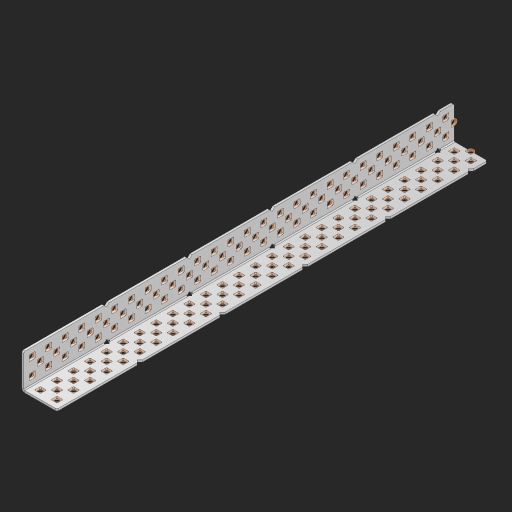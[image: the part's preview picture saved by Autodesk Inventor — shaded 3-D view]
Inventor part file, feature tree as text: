
AUTODESK INVENTOR PART (.ipt)
format: ipt  version: 2023 (Build 270158000, 158)  size: 1,877,504 bytes
history: native  units: in
note: dims shown in document units (in); Inventor stores cm internally (conversion verified against a paired STEP export)
features: other x162, extrude x154, sheet_metal_op x8, sketch x7, pattern_linear x2, mirror x1, chamfer x1
ambient origin geometry x8: Origin, YZ Plane, XZ Plane, XY Plane, X Axis, Y Axis, Z Axis, Center Point
bodies: Solid1 (feature_tree), Body (feature_tree)
feature tree (335):
  sheet_metal_op  "Flanges"
  sheet_metal_op  "Body Pattern"
  pattern_linear  "Center Pattern"  Spacing1=1.0in  [1 undecoded]
  other  "Arc Length"
  pattern_linear  "Notch Pattern"  Spacing1=0.25in  [1 undecoded]
  other  "Diagonal Plane"
  mirror  "Everything Mirrored"
  chamfer  "End Chamfer"
  sketch  "Sketch1"  dims[d0=1.0in]
  other  "Plate1"
  sketch  "Sketch2"  dims[d1=13.0in]
  other  "Plate2"
  sheet_metal_op  "Bend1"
  sheet_metal_op  "Corner1"
  sketch  "Sketch8"  dims[d2=0.0625in]
  sketch  "Sketch9"  dims[d3=0.0625in]
  other  "Srf91"
  sheet_metal_op  "Body Pattern Sketch"
  other  "Srf92"
  sketch  "Sketch13"  dims[d4=0.0312in]
  sketch  "Sketch15"  dims[d5=0.125in]
  sketch  "Sketch16"  dims[d6=0.0625in d7=1.0in d8=90.0deg d9=0.0312in d10=0.25in d11=0.0625in d12=0.0625in d49=0.182in d50=0.02in d52=0.25in d53=0.0625in d54=0.0in d55=0.172in d56=1.0in d57=0.0in d60=10.2362in d62=0.5in d63=0.7874in d65=0.5in d85=0.1473in d86=0.1782in d89=0.0625in d90=0.0in d91=0.04in d92=0.0491in d95=2.5in d96=0.04in d97=0.25in d98=45.0deg d99=0.25in d106=0.182in d107=0.02in d108=0.5in d110=0.0625in d111=0.0in d112=0.172in d113=0.5in d114=0.0in d117=0.5in d123=0.25in d125=0.25in d126=0.0491in d127=0.1473in d128=0.08in d129=0.04in d130=2.5in]
  other  "Srf786"
  other  "Srf856"
  other  "Srf857"
  other  "Srf858"
  other  "Srf859"
  other  "Srf860"
  other  "Srf861"
  other  "Srf889"
  other  "Srf890"
  other  "Srf891"
  other  "Srf1275"
  other  "Srf1276"
  other  "Srf1278"
  other  "Srf1279"
  other  "Srf1280"
  other  "Srf1281"
  other  "Srf1282"
  other  "Srf1283"
  other  "Srf1277"
  other  "Srf1285"
  other  "Srf1286"
  other  "Srf1287"
  other  "Srf1383"
  other  "Srf1384"
  other  "Srf1385"
  other  "Srf1386"
  other  "Srf1387"
  other  "Srf1388"
  other  "Srf1389"
  other  "Srf1390"
  other  "Srf1391"
  other  "Srf1392"
  other  "Srf1393"
  other  "Srf1394"
  other  "Srf1395"
  other  "Srf1396"
  other  "Srf1397"
  other  "Srf1398"
  other  "Srf1399"
  other  "Srf1400"
  other  "Srf1401"
  other  "Srf1402"
  other  "Srf1403"
  other  "Srf1404"
  other  "Srf1405"
  other  "Srf1406"
  other  "Srf1407"
  other  "Srf1408"
  other  "Srf1409"
  other  "Srf1410"
  other  "Srf1411"
  other  "Srf1412"
  other  "Srf1413"
  other  "Srf1414"
  other  "Srf1415"
  other  "Srf1416"
  other  "Srf1417"
  other  "Srf1418"
  other  "Srf1419"
  other  "Srf1420"
  other  "Srf1421"
  other  "Srf1422"
  other  "Srf1423"
  other  "Srf1424"
  other  "Srf1425"
  other  "Srf1426"
  other  "Srf1445"
  other  "Srf1446"
  other  "Srf1447"
  other  "Srf1448"
  other  "Srf1449"
  other  "Srf1450"
  other  "Srf1451"
  other  "Srf1452"
  other  "Srf1453"
  other  "Srf1454"
  other  "Srf1455"
  other  "Srf1456"
  other  "Srf1457"
  other  "Srf1458"
  other  "Srf1459"
  other  "Srf1460"
  other  "Srf1461"
  other  "Srf1462"
  other  "Srf1463"
  other  "Srf1464"
  other  "Srf1465"
  other  "Srf1466"
  other  "Srf1475"
  other  "Srf1476"
  other  "Srf1477"
  other  "Srf1478"
  other  "Srf1479"
  other  "Srf1480"
  other  "Srf1481"
  other  "Srf1482"
  other  "Srf1483"
  other  "Srf1484"
  other  "Srf1485"
  other  "Srf1486"
  other  "Srf1487"
  other  "Srf1488"
  other  "Srf1489"
  other  "Srf1490"
  other  "Srf1491"
  other  "Srf1492"
  other  "Srf1493"
  other  "Srf1494"
  other  "Srf1495"
  other  "Srf1496"
  other  "Srf1497"
  other  "Srf1498"
  other  "Srf1499"
  other  "Srf1500"
  other  "Srf1501"
  other  "Srf1502"
  other  "Srf1503"
  other  "Srf1504"
  other  "Srf1505"
  other  "Srf1506"
  other  "Srf1507"
  other  "Srf1508"
  other  "Srf1509"
  other  "Srf1510"
  other  "Srf1511"
  other  "Srf1512"
  other  "Srf1513"
  other  "Srf1514"
  other  "Srf1515"
  other  "Srf1516"
  other  "Srf1517"
  other  "Srf1518"
  other  "Srf1537"
  other  "Srf1538"
  other  "Srf1539"
  other  "Srf1540"
  other  "Srf1541"
  other  "Srf1542"
  other  "Srf1543"
  other  "Srf1544"
  other  "Srf1545"
  other  "Srf1546"
  other  "Srf1547"
  other  "Srf1548"
  other  "Srf1549"
  other  "Srf1550"
  other  "Srf1551"
  other  "Srf1552"
  other  "Srf1553"
  other  "Srf1554"
  other  "Srf1555"
  other  "Srf1556"
  other  "Srf1557"
  other  "Srf1558"
  sheet_metal_op  "Body Stamp"
  sheet_metal_op  "Body Circle"
  other  "Center Stamp"
  other  "Center Circle"
  sheet_metal_op  "Notch"
  extrude  "ExtrusionSrf92"  Depth=0.0625in
  extrude  "ExtrusionSrf856"  Depth=0.0625in
  extrude  "ExtrusionSrf857"  Depth=0.182in
  extrude  "ExtrusionSrf858"  Depth=0.02in
  extrude  "ExtrusionSrf859"  Depth=0.25in
  extrude  "ExtrusionSrf860"  Depth=0.0625in
  extrude  "ExtrusionSrf861"  TaperAngle=0.0deg  [1 undecoded]
  extrude  "ExtrusionSrf889"  Depth=2.5in
  extrude  "ExtrusionSrf890"  Depth=1.0in TaperAngle=0.0deg
  extrude  "ExtrusionSrf891"  Depth=2.5in
  extrude  "ExtrusionSrf1275"  Depth=0.5in
  extrude  "ExtrusionSrf1276"  Depth=2.5in
  extrude  "ExtrusionSrf1277"  Depth=2.5in
  extrude  "ExtrusionSrf1278"  Depth=0.0625in
  extrude  "ExtrusionSrf1279"  Depth=2.5in TaperAngle=0.0deg
  extrude  "ExtrusionSrf1280"  Depth=2.5in
  extrude  "ExtrusionSrf1281"  Depth=0.25in TaperAngle=45.0deg
  extrude  "ExtrusionSrf1282"  Depth=0.25in
  extrude  "ExtrusionSrf1345"  Depth=0.182in
  extrude  "ExtrusionSrf1346"  Depth=0.02in
  extrude  "ExtrusionSrf1347"  Depth=0.5in
  extrude  "ExtrusionSrf1348"  Depth=0.0625in
  extrude  "ExtrusionSrf1383"  TaperAngle=0.0deg  [1 undecoded]
  extrude  "ExtrusionSrf1384"  Depth=2.5in
  extrude  "ExtrusionSrf1385"  Depth=0.5in TaperAngle=0.0deg
  extrude  "ExtrusionSrf1386"  Depth=0.5in
  extrude  "ExtrusionSrf1387"  Depth=0.25in
  extrude  "ExtrusionSrf1388"  Depth=0.25in
  extrude  "ExtrusionSrf1389"  Depth=2.5in
  extrude  "ExtrusionSrf1390"  Depth=2.5in
  extrude  "ExtrusionSrf1391"  Depth=2.5in
  extrude  "ExtrusionSrf1392"  Depth=2.5in
  extrude  "ExtrusionSrf1393"  Depth=2.5in
  extrude  "ExtrusionSrf1394"  [1 undecoded]
  extrude  "ExtrusionSrf1395"  [1 undecoded]
  extrude  "ExtrusionSrf1396"  [1 undecoded]
  extrude  "ExtrusionSrf1397"  [1 undecoded]
  extrude  "ExtrusionSrf1398"  [1 undecoded]
  extrude  "ExtrusionSrf1399"  [1 undecoded]
  extrude  "ExtrusionSrf1400"  [1 undecoded]
  extrude  "ExtrusionSrf1401"  [1 undecoded]
  extrude  "ExtrusionSrf1402"  [1 undecoded]
  extrude  "ExtrusionSrf1403"  [1 undecoded]
  extrude  "ExtrusionSrf1404"  [1 undecoded]
  extrude  "ExtrusionSrf1405"  [1 undecoded]
  extrude  "ExtrusionSrf1406"  [1 undecoded]
  extrude  "ExtrusionSrf1407"  [1 undecoded]
  extrude  "ExtrusionSrf1408"  [1 undecoded]
  extrude  "ExtrusionSrf1409"  [1 undecoded]
  extrude  "ExtrusionSrf1410"  [1 undecoded]
  extrude  "ExtrusionSrf1411"  [1 undecoded]
  extrude  "ExtrusionSrf1412"  [1 undecoded]
  extrude  "ExtrusionSrf1413"  [1 undecoded]
  extrude  "ExtrusionSrf1414"  [1 undecoded]
  extrude  "ExtrusionSrf1415"  [1 undecoded]
  extrude  "ExtrusionSrf1416"  [1 undecoded]
  extrude  "ExtrusionSrf1417"  [1 undecoded]
  extrude  "ExtrusionSrf1418"  [1 undecoded]
  extrude  "ExtrusionSrf1419"  [1 undecoded]
  extrude  "ExtrusionSrf1420"  [1 undecoded]
  extrude  "ExtrusionSrf1421"  [1 undecoded]
  extrude  "ExtrusionSrf1422"  [1 undecoded]
  extrude  "ExtrusionSrf1423"  [1 undecoded]
  extrude  "ExtrusionSrf1424"  [1 undecoded]
  extrude  "ExtrusionSrf1425"  [1 undecoded]
  extrude  "ExtrusionSrf1426"  [1 undecoded]
  extrude  "ExtrusionSrf1445"  [1 undecoded]
  extrude  "ExtrusionSrf1446"  [1 undecoded]
  extrude  "ExtrusionSrf1447"  [1 undecoded]
  extrude  "ExtrusionSrf1448"  [1 undecoded]
  extrude  "ExtrusionSrf1449"  [1 undecoded]
  extrude  "ExtrusionSrf1450"  [1 undecoded]
  extrude  "ExtrusionSrf1451"  [1 undecoded]
  extrude  "ExtrusionSrf1452"  [1 undecoded]
  extrude  "ExtrusionSrf1453"  [1 undecoded]
  extrude  "ExtrusionSrf1454"  [1 undecoded]
  extrude  "ExtrusionSrf1455"  [1 undecoded]
  extrude  "ExtrusionSrf1456"  [1 undecoded]
  extrude  "ExtrusionSrf1457"  [1 undecoded]
  extrude  "ExtrusionSrf1458"  [1 undecoded]
  extrude  "ExtrusionSrf1459"  [1 undecoded]
  extrude  "ExtrusionSrf1460"  [1 undecoded]
  extrude  "ExtrusionSrf1461"  [1 undecoded]
  extrude  "ExtrusionSrf1462"  [1 undecoded]
  extrude  "ExtrusionSrf1463"  [1 undecoded]
  extrude  "ExtrusionSrf1464"  [1 undecoded]
  extrude  "ExtrusionSrf1465"  [1 undecoded]
  extrude  "ExtrusionSrf1466"  [1 undecoded]
  extrude  "ExtrusionSrf1475"  [1 undecoded]
  extrude  "ExtrusionSrf1476"  [1 undecoded]
  extrude  "ExtrusionSrf1477"  [1 undecoded]
  extrude  "ExtrusionSrf1478"  [1 undecoded]
  extrude  "ExtrusionSrf1479"  [1 undecoded]
  extrude  "ExtrusionSrf1480"  [1 undecoded]
  extrude  "ExtrusionSrf1481"  [1 undecoded]
  extrude  "ExtrusionSrf1482"  [1 undecoded]
  extrude  "ExtrusionSrf1483"  [1 undecoded]
  extrude  "ExtrusionSrf1484"  [1 undecoded]
  extrude  "ExtrusionSrf1485"  [1 undecoded]
  extrude  "ExtrusionSrf1486"  [1 undecoded]
  extrude  "ExtrusionSrf1487"  [1 undecoded]
  extrude  "ExtrusionSrf1488"  [1 undecoded]
  extrude  "ExtrusionSrf1489"  [1 undecoded]
  extrude  "ExtrusionSrf1490"  [1 undecoded]
  extrude  "ExtrusionSrf1491"  [1 undecoded]
  extrude  "ExtrusionSrf1492"  [1 undecoded]
  extrude  "ExtrusionSrf1493"  [1 undecoded]
  extrude  "ExtrusionSrf1494"  [1 undecoded]
  extrude  "ExtrusionSrf1495"  [1 undecoded]
  extrude  "ExtrusionSrf1496"  [1 undecoded]
  extrude  "ExtrusionSrf1497"  [1 undecoded]
  extrude  "ExtrusionSrf1498"  [1 undecoded]
  extrude  "ExtrusionSrf1499"  [1 undecoded]
  extrude  "ExtrusionSrf1500"  [1 undecoded]
  extrude  "ExtrusionSrf1501"  [1 undecoded]
  extrude  "ExtrusionSrf1502"  [1 undecoded]
  extrude  "ExtrusionSrf1503"  [1 undecoded]
  extrude  "ExtrusionSrf1504"  [1 undecoded]
  extrude  "ExtrusionSrf1505"  [1 undecoded]
  extrude  "ExtrusionSrf1506"  [1 undecoded]
  extrude  "ExtrusionSrf1507"  [1 undecoded]
  extrude  "ExtrusionSrf1508"  [1 undecoded]
  extrude  "ExtrusionSrf1509"  [1 undecoded]
  extrude  "ExtrusionSrf1510"  [1 undecoded]
  extrude  "ExtrusionSrf1511"  [1 undecoded]
  extrude  "ExtrusionSrf1512"  [1 undecoded]
  extrude  "ExtrusionSrf1513"  [1 undecoded]
  extrude  "ExtrusionSrf1514"  [1 undecoded]
  extrude  "ExtrusionSrf1515"  [1 undecoded]
  extrude  "ExtrusionSrf1516"  [1 undecoded]
  extrude  "ExtrusionSrf1517"  [1 undecoded]
  extrude  "ExtrusionSrf1518"  [1 undecoded]
  extrude  "ExtrusionSrf1537"  [1 undecoded]
  extrude  "ExtrusionSrf1538"  [1 undecoded]
  extrude  "ExtrusionSrf1539"  [1 undecoded]
  extrude  "ExtrusionSrf1540"  [1 undecoded]
  extrude  "ExtrusionSrf1541"  [1 undecoded]
  extrude  "ExtrusionSrf1542"  [1 undecoded]
  extrude  "ExtrusionSrf1543"  [1 undecoded]
  extrude  "ExtrusionSrf1544"  [1 undecoded]
  extrude  "ExtrusionSrf1545"  [1 undecoded]
  extrude  "ExtrusionSrf1546"  [1 undecoded]
  extrude  "ExtrusionSrf1547"  [1 undecoded]
  extrude  "ExtrusionSrf1548"  [1 undecoded]
  extrude  "ExtrusionSrf1549"  [1 undecoded]
  extrude  "ExtrusionSrf1550"  [1 undecoded]
  extrude  "ExtrusionSrf1551"  [1 undecoded]
  extrude  "ExtrusionSrf1552"  [1 undecoded]
  extrude  "ExtrusionSrf1553"  [1 undecoded]
  extrude  "ExtrusionSrf1554"  [1 undecoded]
  extrude  "ExtrusionSrf1555"  [1 undecoded]
  extrude  "ExtrusionSrf1556"  [1 undecoded]
  extrude  "ExtrusionSrf1557"  [1 undecoded]
  extrude  "ExtrusionSrf1558"  [1 undecoded]
note: 125 required parameter values undecoded (feature->parameter linkage not recoverable at this tier; creation-order binding heuristic only, values carry confidence <= 0.55)
